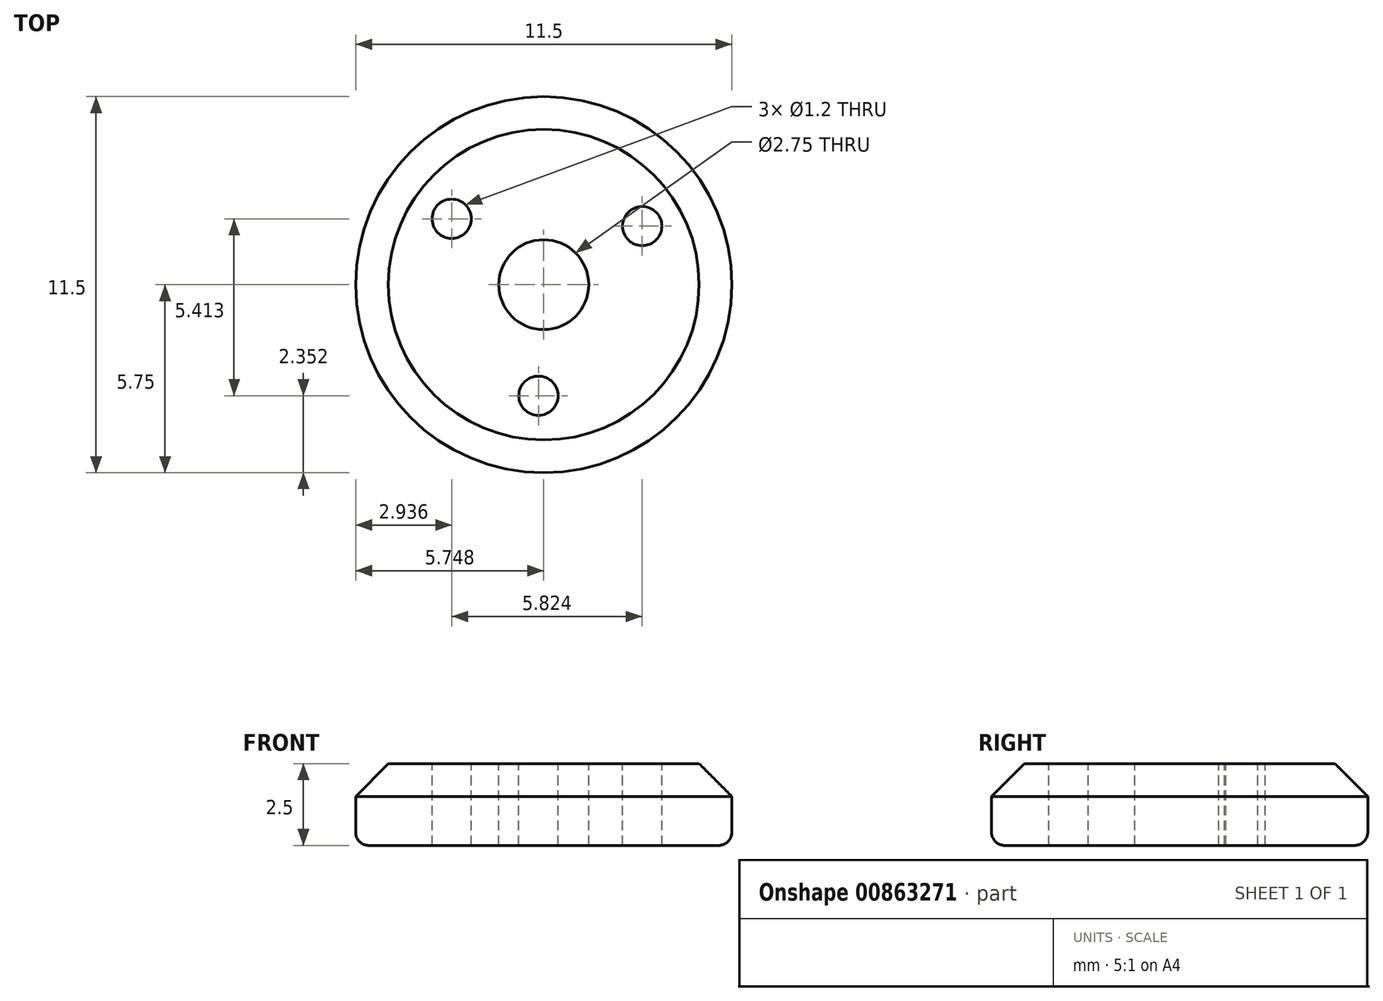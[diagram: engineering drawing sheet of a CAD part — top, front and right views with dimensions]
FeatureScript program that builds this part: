
annotation { "Feature Type Name" : "Feature", "Feature Type Description" : "" }
export const myFeature = defineFeature(function(context is Context, id is Id, definition is map)
    precondition{}
    {
        {
            var Q0;
            Q0=qCreatedBy(makeId("Top.planeOp"),FACE);
            var sketch = newSketch(context, id + "F0", { "sketchPlane" : qUnion([Q0])});
            skCircle(sketch, "E0", {"center": v(-19.33, 0) * mm, "radius": 5.75 * mm});
            skSolve(sketch);
        }
        {
            var Q0;
            Q0 = qSketchRegion(id + "F0", true);
            extrude(context, id + "F1", {"entities" : qUnion([Q0]), "depth" : 2.5 * mm, "offsetDistance" : 25.4 * mm});
        }
        {
            var Q0;
            Q0=makeQuery(id+"F1.opExtrude","CAP_FACE",FACE,{"disambiguationData":[OSD([sQuery(id+"F0.wireOp",EDGE,"E0")])],"isStart":false});
            var sketch = newSketch(context, id + "F2", { "sketchPlane" : qUnion([Q0])});
            skCircle(sketch, "E1", {"center": v(-19.33, 0) * mm, "radius": 1.38 * mm});
            skSolve(sketch);
        }
        {
            var Q0;
            Q0 = qSketchRegion(id + "F2", true);
            extrude(context, id + "F3", {"entities" : qUnion([Q0]), "operationType" : NewBodyOperationType.REMOVE, "oppositeDirection" : true, "depth" : 25.4 * mm, "offsetDistance" : 25.4 * mm});
        }
        {
            var Q0;
            Q0=makeQuery(id+"F1.opExtrude","CAP_FACE",FACE,{"disambiguationData":[OSD([sQuery(id+"F0.wireOp",EDGE,"E0")])],"isStart":false});
            var sketch = newSketch(context, id + "F4", { "sketchPlane" : qUnion([Q0])});
            skCircle(sketch, "E2", {"center": v(-22.14, 2.01) * mm, "radius": 0.6 * mm});
            skSolve(sketch);
        }
        {
            var Q0;
            Q0 = qSketchRegion(id + "F4", true);
            extrude(context, id + "F5", {"entities" : qUnion([Q0]), "operationType" : NewBodyOperationType.REMOVE, "oppositeDirection" : true, "depth" : 25.4 * mm, "offsetDistance" : 25.4 * mm});
        }
        {
            var Q0;
            Q0=makeQuery(id+"F1.opExtrude","CAP_FACE",FACE,{"disambiguationData":[OSD([sQuery(id+"F0.wireOp",EDGE,"E0")])],"isStart":false});
            var sketch = newSketch(context, id + "F6", { "sketchPlane" : qUnion([Q0])});
            skCircle(sketch, "E3", {"center": v(-19.5, -3.4) * mm, "radius": 0.6 * mm});
            skSolve(sketch);
        }
        {
            var Q0;
            Q0 = qSketchRegion(id + "F6", true);
            extrude(context, id + "F7", {"entities" : qUnion([Q0]), "operationType" : NewBodyOperationType.REMOVE, "oppositeDirection" : true, "depth" : 25.4 * mm, "offsetDistance" : 25.4 * mm});
        }
        {
            var Q0;
            Q0=makeQuery(id+"F1.opExtrude","CAP_FACE",FACE,{"disambiguationData":[OSD([sQuery(id+"F0.wireOp",EDGE,"E0")])],"isStart":false});
            var sketch = newSketch(context, id + "F8", { "sketchPlane" : qUnion([Q0])});
            skCircle(sketch, "E4", {"center": v(-16.32, 1.8) * mm, "radius": 0.6 * mm});
            skSolve(sketch);
        }
        {
            var Q0;
            Q0=makeQuery(id+"F8.imprint","IMPRINT",FACE,{"disambiguationData":[TD([[makeQuery(id+"F8.imprint","IMPRINT",EDGE,{"derivedFrom":sQuery(id+"F8.wireOp",EDGE,"E4")}),1.0]])]});
            extrude(context, id + "F9", {"entities" : qUnion([Q0]), "operationType" : NewBodyOperationType.REMOVE, "oppositeDirection" : true, "depth" : 25.4 * mm, "offsetDistance" : 25.4 * mm});
        }
        {
            var Q0;
            Q0=makeQuery(id+"F1.opExtrude","CAP_EDGE",EDGE,{"disambiguationData":[OSD([sQuery(id+"F0.wireOp",EDGE,"E0")])],"isStart":false});
            chamfer(context, id + "F10", {"entities" : qUnion([Q0]), "width" : 1 * mm, "tangentPropagation" : true});
        }
        {
            var Q0;
            Q0=makeQuery(id+"F1.opExtrude","CAP_EDGE",EDGE,{"disambiguationData":[OSD([sQuery(id+"F0.wireOp",EDGE,"E0")])],"isStart":true});
            fillet(context, id + "F11", {"entities" : qUnion([Q0]), "radius" : .4 * mm, "tangentPropagation" : true, "allowEdgeOverflow" : false});
        }
    });
